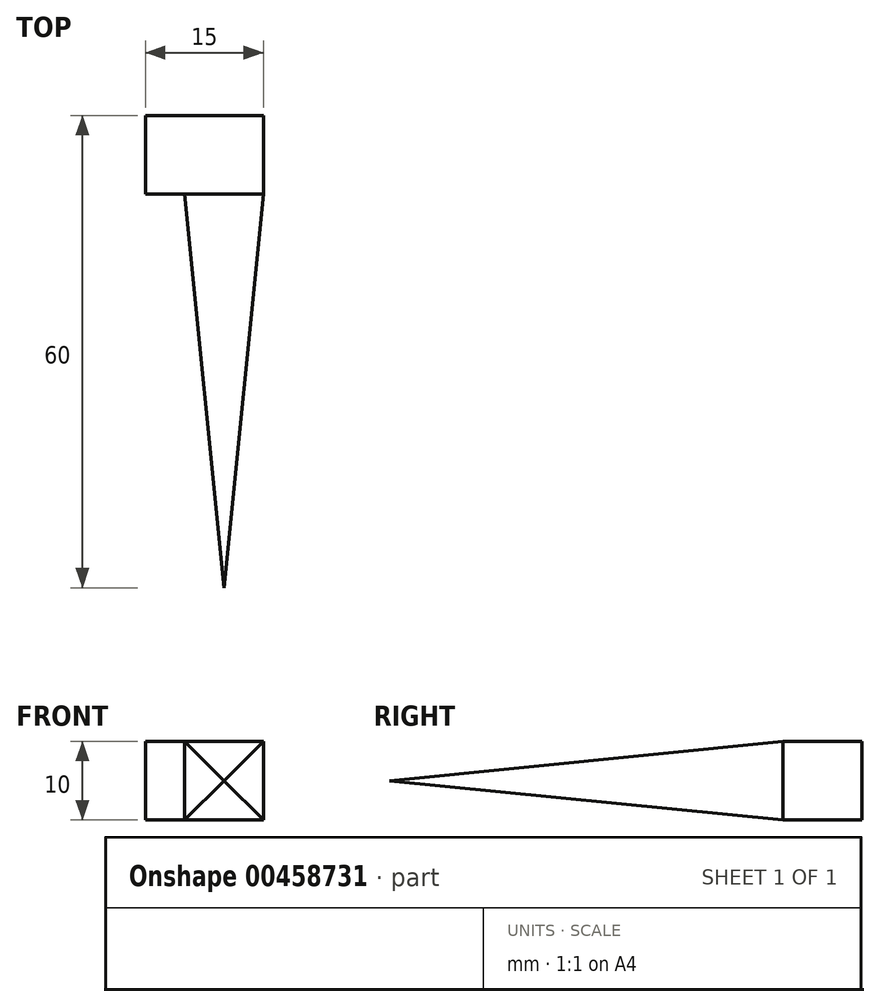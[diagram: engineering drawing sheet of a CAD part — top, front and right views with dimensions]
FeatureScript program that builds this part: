
annotation { "Feature Type Name" : "Feature", "Feature Type Description" : "" }
export const myFeature = defineFeature(function(context is Context, id is Id, definition is map)
    precondition{}
    {
        {
            var Q0;
            Q0=qCreatedBy(makeId("Top.planeOp"),FACE);
            var sketch = newSketch(context, id + "F0", { "sketchPlane" : qUnion([Q0])});
            skLineSegment(sketch, "E0.bottom", {"start": v(0, 0) * mm, "end": v(-15, 0) * mm});
            skLineSegment(sketch, "E0.top", {"start": v(0, 10) * mm, "end": v(-15, 10) * mm});
            skLineSegment(sketch, "E0.left", {"start": v(0, 0) * mm, "end": v(0, 10) * mm});
            skLineSegment(sketch, "E0.right", {"start": v(-15, 0) * mm, "end": v(-15, 10) * mm});
            skLineSegment(sketch, "E1.bottom", {"start": v(0, 10) * mm, "end": v(-10, 10) * mm});
            skLineSegment(sketch, "E1.top", {"start": v(0, -50) * mm, "end": v(-10, -50) * mm});
            skLineSegment(sketch, "E1.left", {"start": v(0, 10) * mm, "end": v(0, -50) * mm});
            skLineSegment(sketch, "E1.right", {"start": v(-10, 10) * mm, "end": v(-10, -50) * mm});
            skSolve(sketch);
        }
        {
            var Q0;
            Q0 = qSketchRegion(id + "F0", true);
            extrude(context, id + "F1", {"entities" : qUnion([Q0]), "depth" : 10 * mm, "offsetDistance" : 25 * mm});
        }
        {
            var Q0;
            Q0=makeQuery(id+"F1.opExtrude","CAP_EDGE",EDGE,{"disambiguationData":[OSD([sQuery(id+"F0.wireOp",EDGE,"E1.top")])],"isStart":false});
            var Q1;
            Q1=makeQuery(id+"F1.opExtrude","SWEPT_EDGE",EDGE,{"disambiguationData":[OSD([sQuery(id+"F0.wireOp",EDGE,"E1.top"),sQuery(id+"F0.wireOp",EDGE,"E1.right")])]});
            var Q2;
            Q2=makeQuery(id+"F1.opExtrude","CAP_EDGE",EDGE,{"disambiguationData":[OSD([sQuery(id+"F0.wireOp",EDGE,"E1.top")])],"isStart":true});
            var Q3;
            Q3=makeQuery(id+"F1.opExtrude","SWEPT_EDGE",EDGE,{"disambiguationData":[OSD([sQuery(id+"F0.wireOp",EDGE,"E1.top"),sQuery(id+"F0.wireOp",EDGE,"E1.left")])]});
            chamfer(context, id + "F2", {"entities" : qUnion([Q0, Q1, Q2, Q3]), "chamferType" : ChamferType.TWO_OFFSETS, "width1" : 5 * mm, "oppositeDirection" : false, "width2" : 50 * mm});
        }
    });
